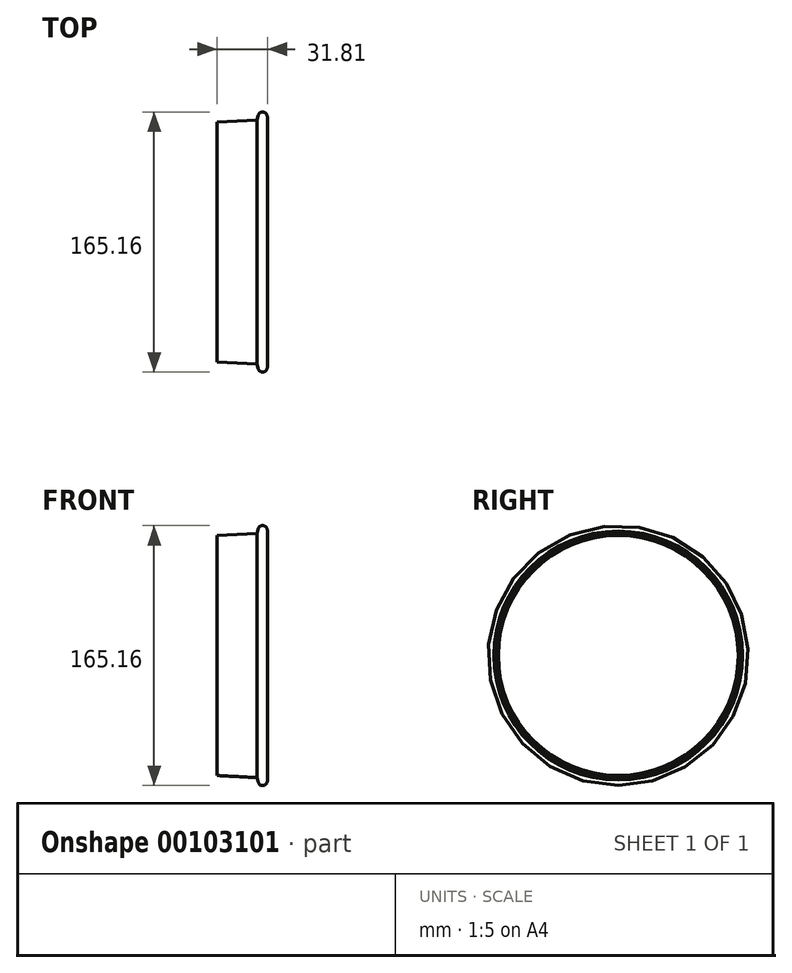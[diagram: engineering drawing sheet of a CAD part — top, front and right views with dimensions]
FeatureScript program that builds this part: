
annotation { "Feature Type Name" : "Feature", "Feature Type Description" : "" }
export const myFeature = defineFeature(function(context is Context, id is Id, definition is map)
    precondition{}
    {
        {
            var Q0;
            Q0=qCreatedBy(makeId("Front.planeOp"),FACE);
            var sketch = newSketch(context, id + "F0", { "sketchPlane" : qUnion([Q0])});
            skLineSegment(sketch, "E0", {"start": v(0, 0) * mm, "end": v(0, 76.2) * mm});
            skLineSegment(sketch, "E1", {"start": v(0, 76.2) * mm, "end": v(25.4, 77.53) * mm});
            skLineSegment(sketch, "E2", {"start": v(25.4, 77.53) * mm, "end": v(25.98, 80.24) * mm});
            skLineSegment(sketch, "E3", {"start": v(31.75, 79.01) * mm, "end": v(31.75, 0) * mm});
            skLineSegment(sketch, "E4", {"start": v(0, 0) * mm, "end": v(31.75, 0) * mm});
            skArc(sketch, "E5", {"start": v(25.98, 80.24) * mm, "mid": v(29.48, 82.51) * mm, "end": v(31.75, 79.01) * mm});
            skSolve(sketch);
        }
        {
            var Q0;
            Q0=sQuery(id+"F0.wireOp",EDGE,"E0");
            var Q1;
            Q1=sQuery(id+"F0.wireOp",EDGE,"E3");
            var Q2;
            Q2=sQuery(id+"F0.wireOp",EDGE,"lBPSAKCK-LcUe-H9xs-P61N-5DQNpd9Jokof");
            var Q3;
            Q3=sQuery(id+"F0.wireOp",EDGE,"E2");
            var Q4;
            Q4=sQuery(id+"F0.wireOp",EDGE,"E1");
            var Q5;
            Q5=sQuery(id+"F0.wireOp",EDGE,"E5");
            var Q6;
            Q6=sQuery(id+"F0.wireOp",EDGE,"E4");
            revolve(context, id + "F1", {"bodyType" : ToolBodyType.SURFACE, "surfaceEntities" : qUnion([Q0, Q1, Q2, Q3, Q4, Q5]), "axis" : qUnion([Q6]), "revolveType" : RevolveType.FULL});
        }
    });
